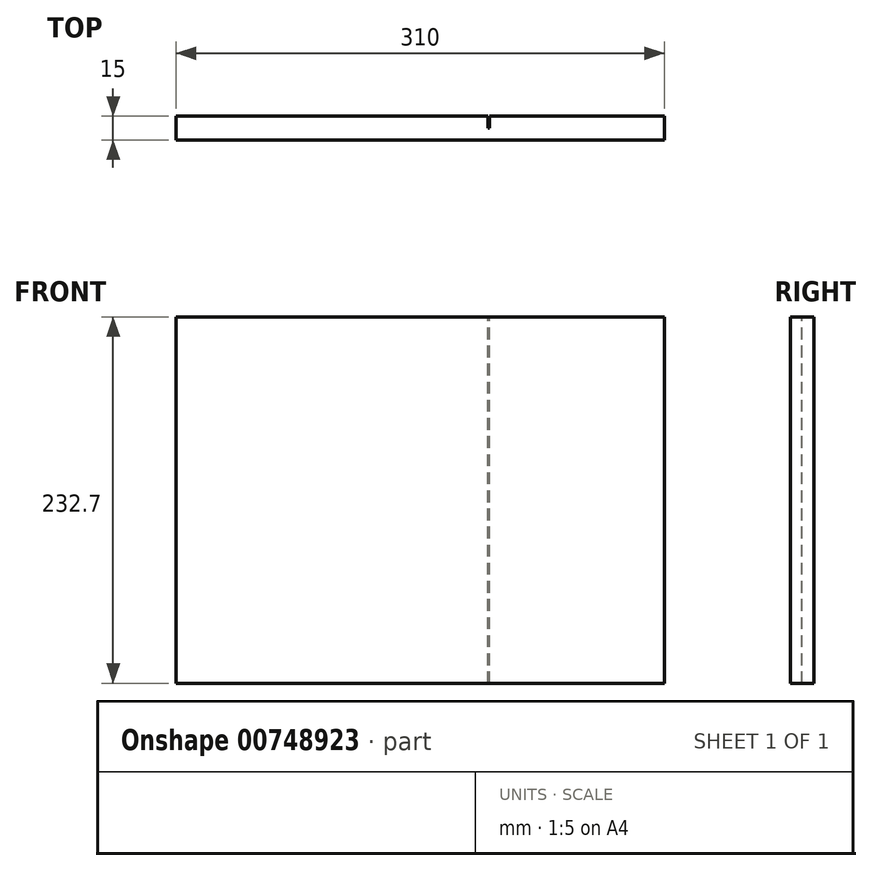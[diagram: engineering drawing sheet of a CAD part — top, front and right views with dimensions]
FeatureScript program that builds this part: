
annotation { "Feature Type Name" : "Feature", "Feature Type Description" : "" }
export const myFeature = defineFeature(function(context is Context, id is Id, definition is map)
    precondition{}
    {
        {
            var Q0;
            Q0=qCreatedBy(makeId("Top.planeOp"),FACE);
            var sketch = newSketch(context, id + "F0", { "sketchPlane" : qUnion([Q0])});
            skLineSegment(sketch, "E0.top", {"start": v(28.13, -7.5) * mm, "end": v(-281.87, -7.5) * mm});
            skLineSegment(sketch, "E0.left", {"start": v(28.13, 7.5) * mm, "end": v(28.13, -7.5) * mm});
            skLineSegment(sketch, "E1", {"start": v(-82.87, 7.5) * mm, "end": v(-82.87, 0) * mm});
            skLineSegment(sketch, "E2", {"start": v(-82.87, 0) * mm, "end": v(-83.87, 0) * mm});
            skLineSegment(sketch, "E3", {"start": v(-83.87, 0) * mm, "end": v(-83.87, 7.5) * mm});
            skLineSegment(sketch, "E4.trimOffspring", {"start": v(-281.87, 7.5) * mm, "end": v(-83.87, 7.5) * mm});
            skLineSegment(sketch, "E5", {"start": v(-281.87, 7.5) * mm, "end": v(-281.87, -7.5) * mm});
            skLineSegment(sketch, "E6", {"start": v(28.13, 7.5) * mm, "end": v(-82.87, 7.5) * mm});
            skSolve(sketch);
        }
        {
            var Q0;
            Q0=makeQuery(id+"F0.imprint","IMPRINT",FACE,{"disambiguationData":[TD([[makeQuery(id+"F0.imprint","IMPRINT",EDGE,{"derivedFrom":sQuery(id+"F0.wireOp",EDGE,"E0.top")}),-1.0]])]});
            extrude(context, id + "F1", {"entities" : qUnion([Q0]), "oppositeDirection" : true, "depth" : 232.7 * mm, "offsetDistance" : 25 * mm, "symmetric" : true});
        }
    });
